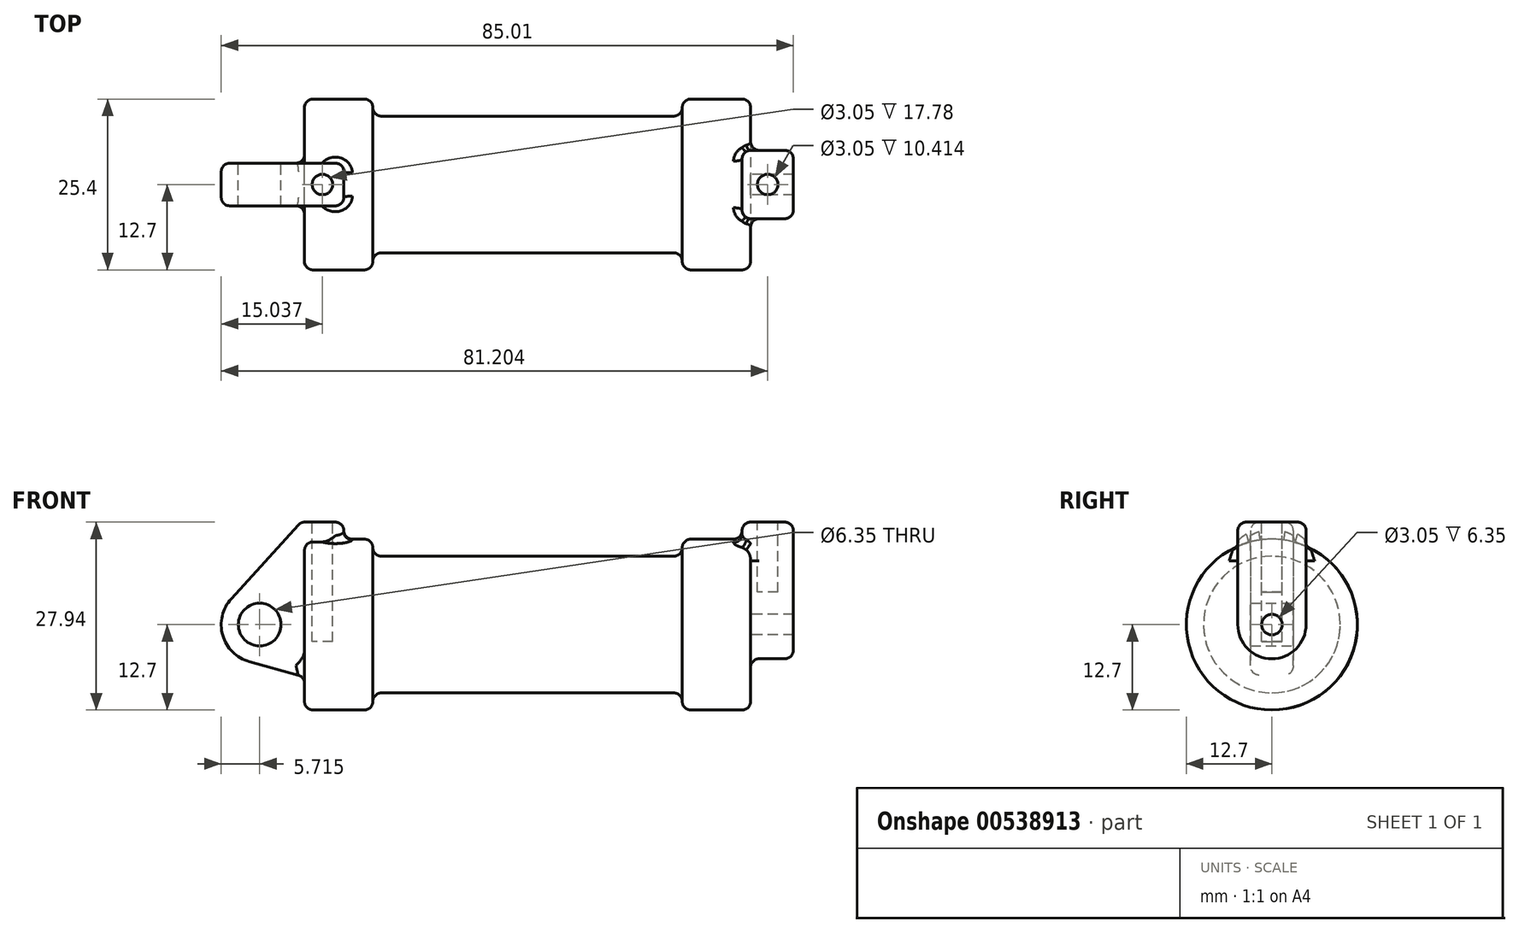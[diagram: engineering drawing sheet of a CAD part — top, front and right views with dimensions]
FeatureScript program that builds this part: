
annotation { "Feature Type Name" : "Feature", "Feature Type Description" : "" }
export const myFeature = defineFeature(function(context is Context, id is Id, definition is map)
    precondition{}
    {
        {
            var Q0;
            Q0=qCreatedBy(makeId("Front.planeOp"),FACE);
            var sketch = newSketch(context, id + "F0", { "sketchPlane" : qUnion([Q0])});
            skLineSegment(sketch, "E0", {"start": v(0, 0) * mm, "end": v(0, 12.7) * mm});
            skLineSegment(sketch, "E1", {"start": v(0, 12.7) * mm, "end": v(10.16, 12.7) * mm});
            skLineSegment(sketch, "E2", {"start": v(10.16, 12.7) * mm, "end": v(10.16, 10.16) * mm});
            skLineSegment(sketch, "E3", {"start": v(10.16, 10.16) * mm, "end": v(56.13, 10.16) * mm});
            skLineSegment(sketch, "E4", {"start": v(56.13, 10.16) * mm, "end": v(56.13, 12.7) * mm});
            skLineSegment(sketch, "E5", {"start": v(56.13, 12.7) * mm, "end": v(66.3, 12.7) * mm});
            skLineSegment(sketch, "E6", {"start": v(66.3, 12.7) * mm, "end": v(66.3, 0) * mm});
            skLineSegment(sketch, "E7", {"start": v(66.3, 0) * mm, "end": v(0, 0) * mm});
            skLineSegment(sketch, "E8", {"start": v(5.84, 15.24) * mm, "end": v(-0.5, 15.24) * mm});
            skLineSegment(sketch, "E9", {"start": v(-0.5, 15.24) * mm, "end": v(-10.88, 3.85) * mm});
            skLineSegment(sketch, "E10", {"start": v(0, 0) * mm, "end": v(-6.65, 0) * mm});
            skCircle(sketch, "E11", {"center": v(-6.65, 0) * mm, "radius": 5.72 * mm});
            skCircle(sketch, "E12", {"center": v(-6.65, 0) * mm, "radius": 3.18 * mm});
            skLineSegment(sketch, "E13", {"start": v(5.84, 15.24) * mm, "end": v(5.84, -9.4) * mm});
            skLineSegment(sketch, "E14", {"start": v(5.84, -9.4) * mm, "end": v(-8.18, -5.5) * mm});
            skSolve(sketch);
        }
        {
            var Q0;
            {var subQ0=sQuery(id+"F0.wireOp",EDGE,"E0");Q0=makeQuery(id+"F0.imprint","IMPRINT",FACE,{"disambiguationData":[TD([[makeQuery(id+"F0.imprint","IMPRINT",EDGE,{"derivedFrom":subQ0}),-1.0]])]});}
            var Q1;
            {var subQ0=sQuery(id+"F0.wireOp",EDGE,"E2");Q1=makeQuery(id+"F0.imprint","IMPRINT",FACE,{"disambiguationData":[TD([[makeQuery(id+"F0.imprint","IMPRINT",EDGE,{"derivedFrom":subQ0}),-1.0]])]});}
            var Q2;
            Q2=sQuery(id+"F0.wireOp",EDGE,"E7");
            revolve(context, id + "F1", {"entities" : qUnion([Q0, Q1]), "axis" : qUnion([Q2]), "revolveType" : RevolveType.FULL});
        }
        {
            var Q0;
            {var subQ0=sQuery(id+"F0.wireOp",EDGE,"E0");Q0=makeQuery(id+"F0.imprint","IMPRINT",FACE,{"disambiguationData":[TD([[makeQuery(id+"F0.imprint","IMPRINT",EDGE,{"derivedFrom":subQ0}),-1.0]])]});}
            var Q1;
            {var subQ1=sQuery(id+"F0.wireOp",EDGE,"E0");Q1=makeQuery(id+"F0.imprint","IMPRINT",FACE,{"disambiguationData":[TD([[makeQuery(id+"F0.imprint","IMPRINT",EDGE,{"derivedFrom":subQ1}),1.0]])]});}
            var Q2;
            {var subQ5=sQuery(id+"F0.wireOp",EDGE,"E12");Q2=makeQuery(id+"F0.imprint","IMPRINT",FACE,{"disambiguationData":[TD([[makeQuery(id+"F0.imprint","IMPRINT",EDGE,{"derivedFrom":subQ5}),-1.0]])]});}
            var Q3;
            {var subQ0=sQuery(id+"F0.wireOp",EDGE,"E14");Q3=makeQuery(id+"F0.imprint","IMPRINT",FACE,{"disambiguationData":[TD([[makeQuery(id+"F0.imprint","IMPRINT",EDGE,{"derivedFrom":subQ0}),-1.0]])]});}
            extrude(context, id + "F2", {"entities" : qUnion([Q0, Q1, Q2, Q3]), "operationType" : NewBodyOperationType.ADD, "endBound" : BoundingType.SYMMETRIC, "depth" : 6.35 * mm, "offsetDistance" : 25.4 * mm});
        }
        {
            var Q0;
            Q0=makeQuery(id+"F1.opRevolve","SWEPT_FACE",FACE,{"disambiguationData":[OSD([sQuery(id+"F0.wireOp",EDGE,"E6")])]});
            var sketch = newSketch(context, id + "F3", { "sketchPlane" : qUnion([Q0])});
            skCircle(sketch, "E15", {"center": v(0, 0) * mm, "radius": 1.52 * mm});
            skCircle(sketch, "E16", {"center": v(0, 0) * mm, "radius": 5.08 * mm});
            skLineSegment(sketch, "E17", {"start": v(5.08, 0) * mm, "end": v(5.08, 15.24) * mm});
            skLineSegment(sketch, "E18", {"start": v(5.08, 15.24) * mm, "end": v(-5.08, 15.24) * mm});
            skLineSegment(sketch, "E19", {"start": v(-5.08, 15.24) * mm, "end": v(-5.08, 0) * mm});
            skSolve(sketch);
        }
        {
            var Q0;
            {var subQ0=sQuery(id+"F3.wireOp",EDGE,"E18");Q0=makeQuery(id+"F3.imprint","IMPRINT",FACE,{"disambiguationData":[TD([[makeQuery(id+"F3.imprint","IMPRINT",EDGE,{"derivedFrom":subQ0}),1.0]])]});}
            var Q1;
            {var subQ0=sQuery(id+"F3.wireOp",EDGE,"E17");var subQ1=sQuery(id+"F3.wireOp",EDGE,"E16");var subQ2=makeQuery(id+"F3.imprint","INTERSECT",VERTEX,{"derivedFrom":[subQ1,subQ0]});Q1=makeQuery(id+"F3.imprint","IMPRINT",FACE,{"disambiguationData":[TD([[makeQuery(id+"F3.imprint","IMPRINT",EDGE,{"disambiguationData":[TD([[subQ2,-1.0]])],"derivedFrom":subQ1}),-1.0]])]});}
            var Q2;
            Q2=makeQuery(id+"F3.imprint","IMPRINT",FACE,{"disambiguationData":[TD([[makeQuery(id+"F3.imprint","IMPRINT",EDGE,{"derivedFrom":sQuery(id+"F3.wireOp",EDGE,"E15")}),-1.0]])]});
            extrude(context, id + "F4", {"entities" : qUnion([Q0, Q1, Q2]), "operationType" : NewBodyOperationType.ADD, "depth" : 6.35 * mm, "offsetDistance" : 25.4 * mm, "hasSecondDirection" : true, "secondDirectionOppositeDirection" : true, "secondDirectionDepth" : 1.27 * mm});
        }
        {
            var Q0;
            Q0=makeQuery(id+"F4.opExtrude","SWEPT_FACE",FACE,{"disambiguationData":[OSD([sQuery(id+"F3.wireOp",EDGE,"E18")])]});
            var sketch = newSketch(context, id + "F5", { "sketchPlane" : qUnion([Q0])});
            skCircle(sketch, "E20", {"center": v(68.83, 0) * mm, "radius": 1.52 * mm});
            skPoint(sketch, "E20.centerSnap0", {"position": v(72.64, 0) * mm});
            skSolve(sketch);
        }
        {
            var Q0;
            Q0=makeQuery(id+"F2.opExtrude","SWEPT_FACE",FACE,{"disambiguationData":[OSD([sQuery(id+"F0.wireOp",EDGE,"E8")])]});
            var sketch = newSketch(context, id + "F6", { "sketchPlane" : qUnion([Q0])});
            skCircle(sketch, "E21", {"center": v(2.67, 0) * mm, "radius": 1.52 * mm});
            skPoint(sketch, "E21.centerSnap0", {"position": v(5.84, 0) * mm});
            skSolve(sketch);
        }
        {
            var Q0;
            Q0=makeQuery(id+"F6.imprint","IMPRINT",FACE,{"disambiguationData":[TD([[makeQuery(id+"F6.imprint","IMPRINT",EDGE,{"derivedFrom":sQuery(id+"F6.wireOp",EDGE,"E21")}),1.0]])]});
            extrude(context, id + "F7", {"entities" : qUnion([Q0]), "operationType" : NewBodyOperationType.REMOVE, "oppositeDirection" : true, "depth" : 17.78 * mm, "offsetDistance" : 25.4 * mm});
        }
        {
            var Q0;
            Q0=makeQuery(id+"F5.imprint","IMPRINT",FACE,{"disambiguationData":[TD([[makeQuery(id+"F5.imprint","IMPRINT",EDGE,{"derivedFrom":sQuery(id+"F5.wireOp",EDGE,"E20")}),1.0]])]});
            extrude(context, id + "F8", {"entities" : qUnion([Q0]), "operationType" : NewBodyOperationType.REMOVE, "oppositeDirection" : true, "depth" : 10.4 * mm, "offsetDistance" : 25.4 * mm});
        }
        {
            var Q0;
            Q0=makeQuery(id+"F1.opRevolve","SWEPT_EDGE",EDGE,{"disambiguationData":[OSD([sQuery(id+"F0.wireOp",EDGE,"E0"),sQuery(id+"F0.wireOp",EDGE,"E1")])]});
            var Q1;
            Q1=makeQuery(id+"F1.opRevolve","SWEPT_EDGE",EDGE,{"disambiguationData":[OSD([sQuery(id+"F0.wireOp",EDGE,"E1"),sQuery(id+"F0.wireOp",EDGE,"E2")])]});
            var Q2;
            Q2=makeQuery(id+"F1.opRevolve","SWEPT_EDGE",EDGE,{"disambiguationData":[OSD([sQuery(id+"F0.wireOp",EDGE,"E2"),sQuery(id+"F0.wireOp",EDGE,"E3")])]});
            var Q3;
            Q3=makeQuery(id+"F1.opRevolve","SWEPT_EDGE",EDGE,{"disambiguationData":[OSD([sQuery(id+"F0.wireOp",EDGE,"E3"),sQuery(id+"F0.wireOp",EDGE,"E4")])]});
            var Q4;
            Q4=makeQuery(id+"F1.opRevolve","SWEPT_EDGE",EDGE,{"disambiguationData":[OSD([sQuery(id+"F0.wireOp",EDGE,"E4"),sQuery(id+"F0.wireOp",EDGE,"E5")])]});
            var Q5;
            Q5=makeQuery(id+"F1.opRevolve","SWEPT_EDGE",EDGE,{"disambiguationData":[OSD([sQuery(id+"F0.wireOp",EDGE,"E5"),sQuery(id+"F0.wireOp",EDGE,"E6")])]});
            fillet(context, id + "F9", {"entities" : qUnion([Q0, Q1, Q2, Q3, Q4, Q5]), "radius" : 1.27 * mm, "tangentPropagation" : true, "allowEdgeOverflow" : false});
        }
        {
            var Q0;
            Q0=makeQuery(id+"F2.boolean.opBoolean","INTERSECT",EDGE,{"derivedFrom":[makeQuery(id+"F1.opRevolve","SWEPT_FACE",FACE,{"disambiguationData":[OSD([sQuery(id+"F0.wireOp",EDGE,"E1")])]}),makeQuery(id+"F2.opExtrude","SWEPT_FACE",FACE,{"disambiguationData":[OSD([sQuery(id+"F0.wireOp",EDGE,"E13")])]})]});
            var Q1;
            Q1=makeQuery(id+"F2.opExtrude","CAP_EDGE",EDGE,{"disambiguationData":[OSD([sQuery(id+"F0.wireOp",EDGE,"E13")])],"isStart":true});
            var Q2;
            Q2=makeQuery(id+"F2.opExtrude","CAP_EDGE",EDGE,{"disambiguationData":[OSD([sQuery(id+"F0.wireOp",EDGE,"E13")])],"isStart":false});
            var Q3;
            Q3=makeQuery(id+"F2.boolean.opBoolean","INTERSECT",EDGE,{"derivedFrom":[makeQuery(id+"F1.opRevolve","SWEPT_FACE",FACE,{"disambiguationData":[OSD([sQuery(id+"F0.wireOp",EDGE,"E0")])]}),makeQuery(id+"F2.opExtrude","SWEPT_FACE",FACE,{"disambiguationData":[OSD([sQuery(id+"F0.wireOp",EDGE,"E14")])]})]});
            var Q4;
            Q4=makeQuery(id+"F2.opExtrude","SWEPT_EDGE",EDGE,{"disambiguationData":[OSD([sQuery(id+"F0.wireOp",EDGE,"E8"),sQuery(id+"F0.wireOp",EDGE,"E13")])]});
            var Q5;
            Q5=makeQuery(id+"F2.opExtrude","CAP_EDGE",EDGE,{"disambiguationData":[OSD([sQuery(id+"F0.wireOp",EDGE,"E8")])],"isStart":true});
            var Q6;
            Q6=makeQuery(id+"F2.opExtrude","CAP_EDGE",EDGE,{"disambiguationData":[OSD([sQuery(id+"F0.wireOp",EDGE,"E8")])],"isStart":false});
            var Q7;
            Q7=makeQuery(id+"F2.opExtrude","CAP_EDGE",EDGE,{"disambiguationData":[OSD([sQuery(id+"F0.wireOp",EDGE,"E9")])],"isStart":true});
            var Q8;
            Q8=makeQuery(id+"F2.opExtrude","CAP_EDGE",EDGE,{"disambiguationData":[OSD([sQuery(id+"F0.wireOp",EDGE,"E11")])],"isStart":false});
            var Q9;
            Q9=makeQuery(id+"F2.opExtrude","SWEPT_EDGE",EDGE,{"disambiguationData":[OSD([sQuery(id+"F0.wireOp",EDGE,"E8"),sQuery(id+"F0.wireOp",EDGE,"E9")])]});
            fillet(context, id + "F10", {"entities" : qUnion([Q0, Q1, Q2, Q3, Q4, Q5, Q6, Q7, Q8, Q9]), "radius" : 1.27 * mm, "tangentPropagation" : true, "allowEdgeOverflow" : false});
        }
        {
            var Q0;
            Q0=makeQuery(id+"F4.opExtrude","CAP_EDGE",EDGE,{"disambiguationData":[OSD([sQuery(id+"F3.wireOp",EDGE,"E19")])],"isStart":false});
            var Q1;
            Q1=makeQuery(id+"F4.boolean.opBoolean","INTERSECT",EDGE,{"derivedFrom":[makeQuery(id+"F1.opRevolve","SWEPT_FACE",FACE,{"disambiguationData":[OSD([sQuery(id+"F0.wireOp",EDGE,"E6")])]}),makeQuery(id+"F4.opExtrude","SWEPT_FACE",FACE,{"disambiguationData":[OSD([sQuery(id+"F3.wireOp",EDGE,"E19")])]})]});
            var Q2;
            Q2=makeQuery(id+"F4.boolean.opBoolean","INTERSECT",EDGE,{"derivedFrom":[makeQuery(id+"F1.opRevolve","SWEPT_FACE",FACE,{"disambiguationData":[OSD([sQuery(id+"F0.wireOp",EDGE,"E5")])]}),makeQuery(id+"F4.opExtrude","CAP_FACE",FACE,{"disambiguationData":[OSD([sQuery(id+"F3.wireOp",EDGE,"E15"),sQuery(id+"F3.wireOp",EDGE,"E16"),sQuery(id+"F3.wireOp",EDGE,"E17"),sQuery(id+"F3.wireOp",EDGE,"E18"),sQuery(id+"F3.wireOp",EDGE,"E19")])],"isStart":true})]});
            var Q3;
            Q3=makeQuery(id+"F4.opExtrude","CAP_EDGE",EDGE,{"disambiguationData":[OSD([sQuery(id+"F3.wireOp",EDGE,"E17")])],"isStart":true});
            var Q4;
            Q4=makeQuery(id+"F4.opExtrude","CAP_EDGE",EDGE,{"disambiguationData":[OSD([sQuery(id+"F3.wireOp",EDGE,"E19")])],"isStart":true});
            var Q5;
            Q5=makeQuery(id+"F4.opExtrude","SWEPT_EDGE",EDGE,{"disambiguationData":[OSD([sQuery(id+"F3.wireOp",EDGE,"E17"),sQuery(id+"F3.wireOp",EDGE,"E18")])]});
            var Q6;
            Q6=makeQuery(id+"F4.opExtrude","CAP_EDGE",EDGE,{"disambiguationData":[OSD([sQuery(id+"F3.wireOp",EDGE,"E18")])],"isStart":true});
            var Q7;
            Q7=makeQuery(id+"F4.opExtrude","SWEPT_EDGE",EDGE,{"disambiguationData":[OSD([sQuery(id+"F3.wireOp",EDGE,"E18"),sQuery(id+"F3.wireOp",EDGE,"E19")])]});
            var Q8;
            Q8=makeQuery(id+"F4.opExtrude","CAP_EDGE",EDGE,{"disambiguationData":[OSD([sQuery(id+"F3.wireOp",EDGE,"E18")])],"isStart":false});
            fillet(context, id + "F11", {"entities" : qUnion([Q0, Q1, Q2, Q3, Q4, Q5, Q6, Q7, Q8]), "radius" : 1.27 * mm, "tangentPropagation" : true, "allowEdgeOverflow" : false});
        }
    });
